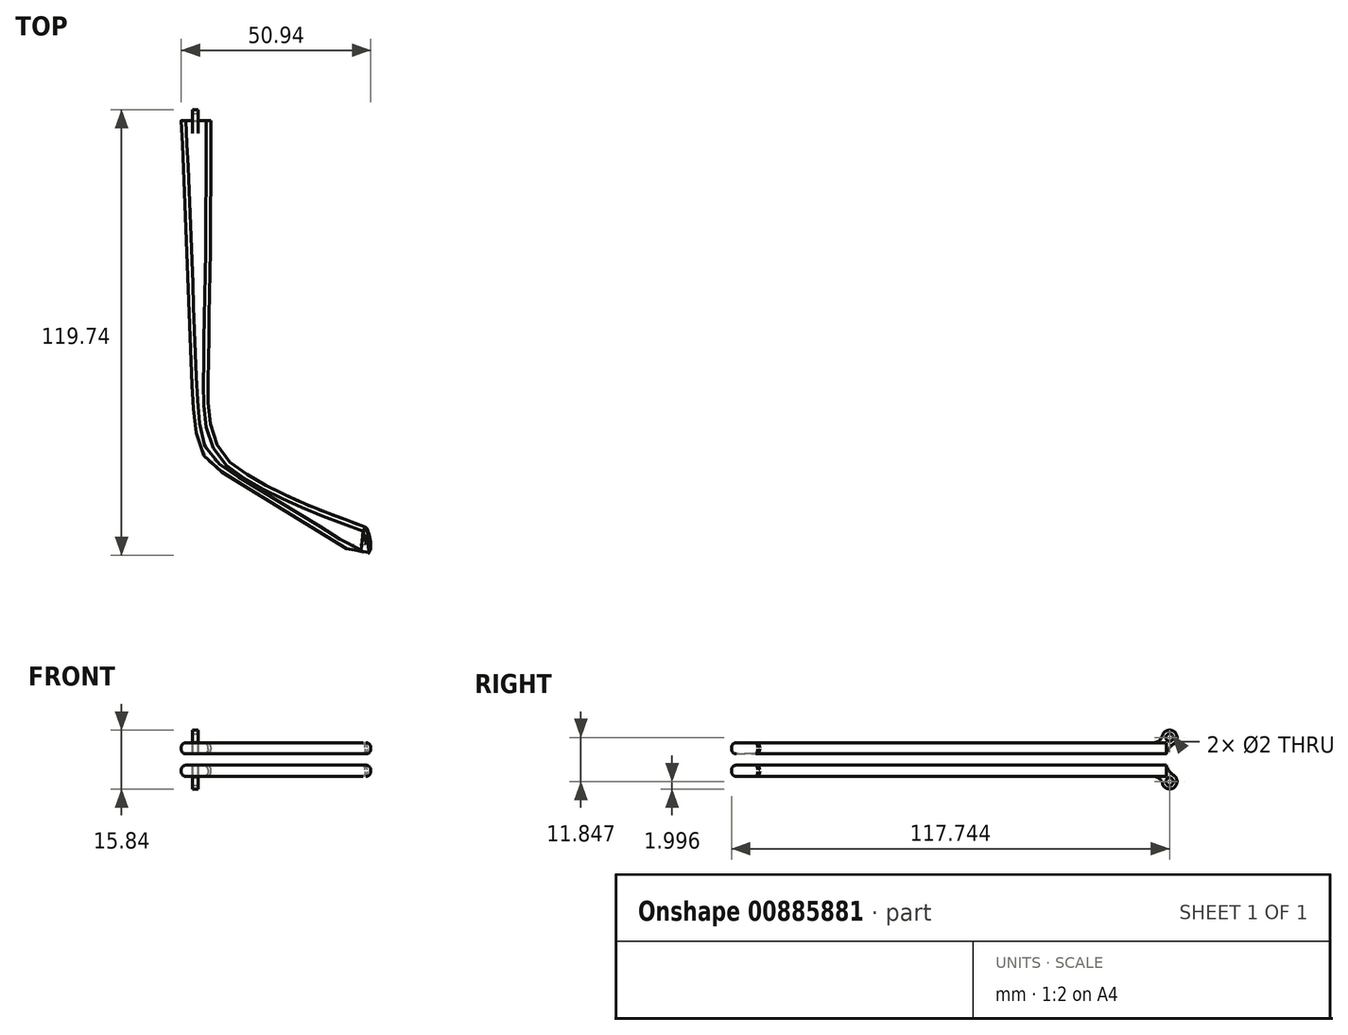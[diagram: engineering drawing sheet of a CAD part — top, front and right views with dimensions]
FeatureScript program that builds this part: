
annotation { "Feature Type Name" : "Feature", "Feature Type Description" : "" }
export const myFeature = defineFeature(function(context is Context, id is Id, definition is map)
    precondition{}
    {
        {
            var Q0;
            Q0=qCreatedBy(makeId("Top.planeOp"),FACE);
            var sketch = newSketch(context, id + "F0", { "sketchPlane" : qUnion([Q0])});
            skLineSegment(sketch, "E0", {"start": v(-22.1, 42.3) * mm, "end": v(-14.1, 42.3) * mm});
            skFitSpline(sketch, "E1", {"points": [v(-14.1, 42.3) * mm, v(-14.1, -39.95) * mm, v(-9.93, -48.55) * mm, v(4.11, -57.47) * mm, v(27.75, -67.1) * mm], "startDerivative": vector(0, -458.2) * mm, "endDerivative": vector(181.4, -66.65) * mm});
            skFitSpline(sketch, "E2", {"points": [v(-22.1, 42.3) * mm, v(-16.6, -46.6) * mm, v(-11.59, -51.84) * mm, v(15.1, -68.26) * mm, v(27.63, -74.42) * mm, v(27.75, -67.1) * mm], "startDerivative": vector(24.32, -503.27) * mm, "endDerivative": vector(-42.38, 107.68) * mm});
            skArc(sketch, "E3.filletArc", {"start": v(27.92, -67.54) * mm, "mid": v(27.69, -67.18) * mm, "end": v(27.33, -66.95) * mm});
            skSolve(sketch);
        }
        {
            var Q0;
            Q0=makeQuery(id+"F0.imprint","IMPRINT",FACE,{"disambiguationData":[TD([[makeQuery(id+"F0.imprint","IMPRINT",EDGE,{"derivedFrom":sQuery(id+"F0.wireOp",EDGE,"E0")}),-1.0]])]});
            extrude(context, id + "F1", {"entities" : qUnion([Q0]), "depth" : 3 * mm, "offsetDistance" : 25.4 * mm});
        }
        {
            var Q0;
            Q0=makeQuery(id+"F1.opExtrude","CAP_EDGE",EDGE,{"disambiguationData":[OSD([sQuery(id+"F0.wireOp",EDGE,"E2")])],"isStart":false});
            var Q1;
            Q1=makeQuery(id+"F1.opExtrude","CAP_EDGE",EDGE,{"disambiguationData":[OSD([sQuery(id+"F0.wireOp",EDGE,"E1")])],"isStart":false});
            var Q2;
            Q2=makeQuery(id+"F1.opExtrude","CAP_EDGE",EDGE,{"disambiguationData":[OSD([sQuery(id+"F0.wireOp",EDGE,"E1")])],"isStart":true});
            var Q3;
            Q3=makeQuery(id+"F1.opExtrude","CAP_EDGE",EDGE,{"disambiguationData":[OSD([sQuery(id+"F0.wireOp",EDGE,"E2")])],"isStart":true});
            fillet(context, id + "F2", {"entities" : qUnion([Q0, Q1, Q2, Q3]), "radius" : 1.27 * mm, "tangentPropagation" : true, "allowEdgeOverflow" : false});
        }
        {
            var Q0;
            Q0=qCreatedBy(makeId("Right.planeOp"),FACE);
            var sketch = newSketch(context, id + "F3", { "sketchPlane" : qUnion([Q0])});
            skCircle(sketch, "E4", {"center": v(56.6, 22.92) * mm, "radius": 1 * mm});
            skCircle(sketch, "E5", {"center": v(56.6, 22.92) * mm, "radius": 2 * mm});
            skLineSegment(sketch, "E6", {"start": v(56.6, 22.92) * mm, "end": v(56.6, 21.92) * mm});
            skSolve(sketch);
        }
        {
            var Q0;
            Q0=makeQuery(id+"F3.imprint","IMPRINT",FACE,{"disambiguationData":[TD([[makeQuery(id+"F3.imprint","IMPRINT",EDGE,{"derivedFrom":sQuery(id+"F3.wireOp",EDGE,"E4")}),-1.0]])]});
            var Q1;
            Q1=sQuery(id+"F3.wireOp",EDGE,"E5");
            extrude(context, id + "F4", {"entities" : qUnion([Q0]), "operationType" : NewBodyOperationType.ADD, "surfaceEntities" : qUnion([Q1]), "oppositeDirection" : true, "depth" : 1.5 * mm, "offsetDistance" : 25.4 * mm});
        }
        {
            var Q0;
            Q0=makeQuery(id+"F1.opExtrude","CAP_EDGE",EDGE,{"disambiguationData":[OSD([sQuery(id+"F0.wireOp",EDGE,"E0")])],"isStart":false});
            cPoint(context, id + "F5", {"entities" : qUnion([Q0]), "parameter" : 0.5});
        }
        {
            var Q0;
            Q0=makeQuery(id+"F4.opExtrude","SWEPT_BODY",BODY,{"disambiguationData":[OSD([sQuery(id+"F3.wireOp",EDGE,"E4"),sQuery(id+"F3.wireOp",EDGE,"E5")])]});
            var Q1;
            Q1=makeQuery(id+"F4.opExtrude","CAP_EDGE",EDGE,{"disambiguationData":[OSD([sQuery(id+"F3.wireOp",EDGE,"E5")])],"isStart":false});
            var Q2;
            Q2 = qCreatedBy(id + "F5" ,VERTEX);
            transform(context, id + "F6", {"entities" : qUnion([Q0]), "transformType" : TransformType.TRANSLATION_3D, "dx" : -17.6 * mm, "dy" : -13.4 * mm, "dz" : -18.52 * mm, "makeCopy" : false});
        }
        {
            var Q0;
            Q0=makeQuery(id+"F4.opExtrude","SWEPT_BODY",BODY,{"disambiguationData":[OSD([sQuery(id+"F3.wireOp",EDGE,"E4"),sQuery(id+"F3.wireOp",EDGE,"E5")])]});
            var Q1;
            Q1=makeQuery(id+"F1.opExtrude","SWEPT_BODY",BODY,{"disambiguationData":[OSD([sQuery(id+"F0.wireOp",EDGE,"E0"),sQuery(id+"F0.wireOp",EDGE,"E1"),sQuery(id+"F0.wireOp",EDGE,"E2")])]});
            booleanBodies(context, id + "F7", {"operationType" : BooleanOperationType.UNION, "tools" : qUnion([Q0, Q1])});
        }
        {
            var Q0;
            Q0=makeQuery(id+"F7.opBoolean","INTERSECT",EDGE,{"derivedFrom":[makeQuery(id+"F1.opExtrude","CAP_FACE",FACE,{"disambiguationData":[OSD([sQuery(id+"F0.wireOp",EDGE,"E0"),sQuery(id+"F0.wireOp",EDGE,"E1"),sQuery(id+"F0.wireOp",EDGE,"E2")])],"isStart":false}),makeQuery(id+"F4.opExtrude","SWEPT_FACE",FACE,{"disambiguationData":[OSD([sQuery(id+"F3.wireOp",EDGE,"E5")])]})]});
            fillet(context, id + "F8", {"entities" : qUnion([Q0]), "radius" : 2.54 * mm, "tangentPropagation" : true, "allowEdgeOverflow" : false});
        }
        {
            var Q0;
            Q0=makeQuery(id+"F4.opExtrude","SWEPT_BODY",BODY,{"disambiguationData":[OSD([sQuery(id+"F3.wireOp",EDGE,"E4"),sQuery(id+"F3.wireOp",EDGE,"E5")])]});
            transform(context, id + "F9", {"entities" : qUnion([Q0]), "transformType" : TransformType.TRANSLATION_3D, "dx" : 0 * mm, "dy" : 0 * mm, "dz" : 1.52 * mm, "makeCopy" : false});
        }
        {
            var Q0;
            Q0=makeQuery(id+"F7.opBoolean","INTERSECT",EDGE,{"derivedFrom":[makeQuery(id+"F1.opExtrude","SWEPT_FACE",FACE,{"disambiguationData":[OSD([sQuery(id+"F0.wireOp",EDGE,"E0")])]}),makeQuery(id+"F4.opExtrude","SWEPT_FACE",FACE,{"disambiguationData":[OSD([sQuery(id+"F3.wireOp",EDGE,"E5")])]})]});
            fillet(context, id + "F10", {"entities" : qUnion([Q0]), "radius" : 5.08 * mm, "tangentPropagation" : true, "allowEdgeOverflow" : false});
        }
        {
            var Q0;
            Q0=makeQuery(id+"F4.opExtrude","SWEPT_BODY",BODY,{"disambiguationData":[OSD([sQuery(id+"F3.wireOp",EDGE,"E4"),sQuery(id+"F3.wireOp",EDGE,"E5")])]});
            var Q1;
            Q1=qCreatedBy(makeId("Top.planeOp"),FACE);
            mirror(context, id + "F11", {"entities" : qUnion([Q0]), "mirrorPlane" : qUnion([Q1])});
        }
    });
